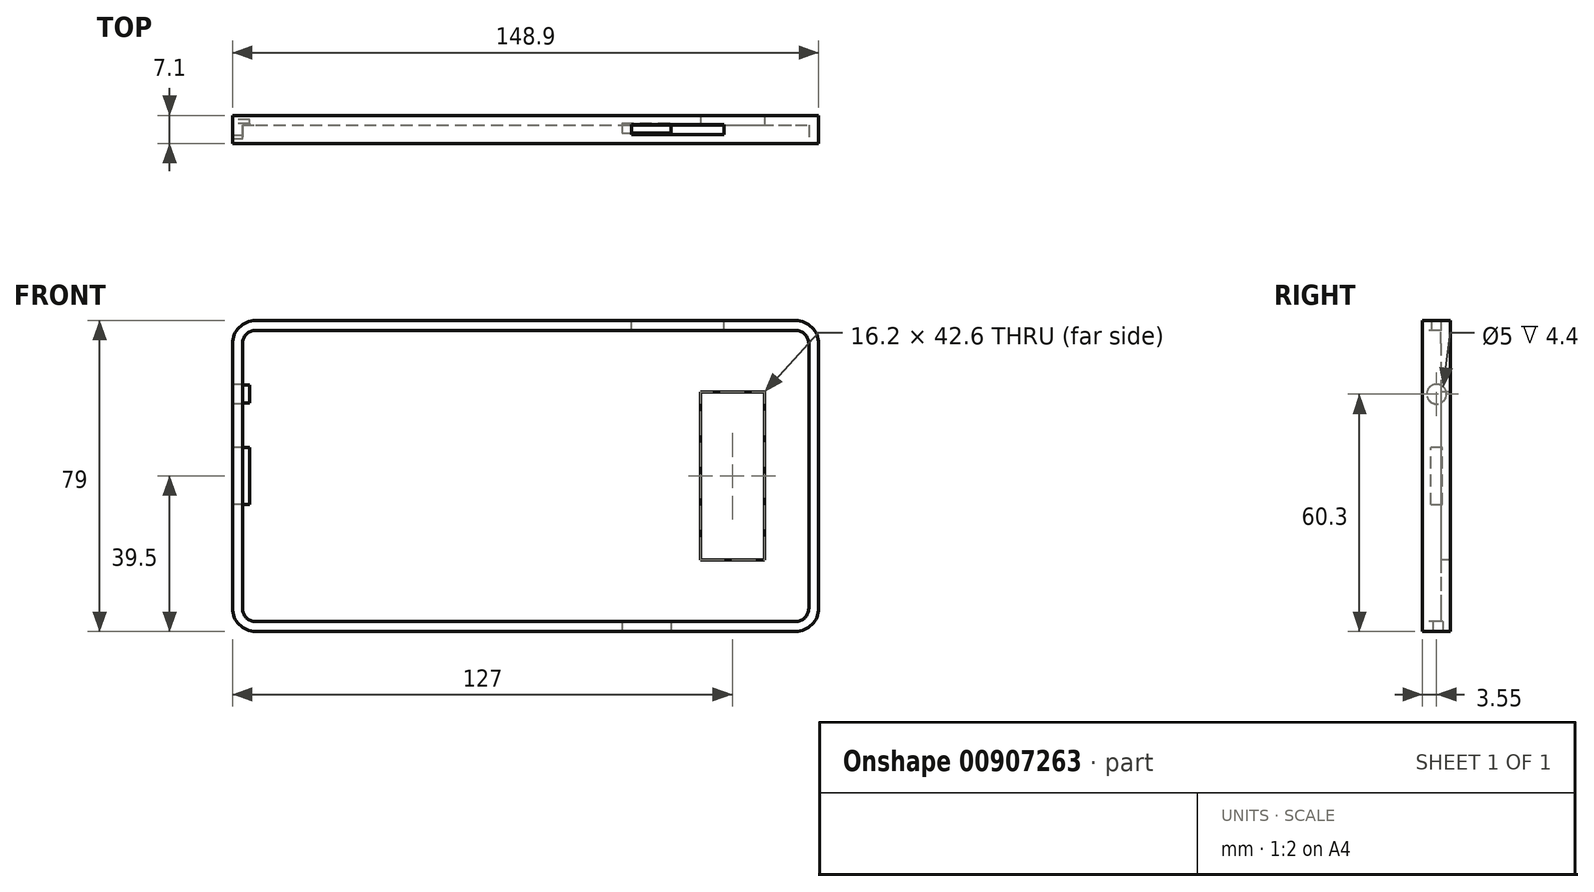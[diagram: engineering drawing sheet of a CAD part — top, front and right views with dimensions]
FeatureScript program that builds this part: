
annotation { "Feature Type Name" : "Feature", "Feature Type Description" : "" }
export const myFeature = defineFeature(function(context is Context, id is Id, definition is map)
    precondition{}
    {
        {
            var Q0;
            Q0=qCreatedBy(makeId("Front.planeOp"),FACE);
            var sketch = newSketch(context, id + "F0", { "sketchPlane" : qUnion([Q0])});
            skLineSegment(sketch, "E0.bottom", {"start": v(-68.55, 39.5) * mm, "end": v(68.55, 39.5) * mm});
            skLineSegment(sketch, "E0.top", {"start": v(-68.55, -39.5) * mm, "end": v(68.55, -39.5) * mm});
            skLineSegment(sketch, "E0.left", {"start": v(-74.45, 33.6) * mm, "end": v(-74.45, -33.6) * mm});
            skLineSegment(sketch, "E0.right", {"start": v(74.45, 33.6) * mm, "end": v(74.45, -33.6) * mm});
            skPoint(sketch, "E0.middle", {"position": v(0, 0) * mm});
            skPoint(sketch, "E1.visualSharp", {"position": v(-74.45, 39.5) * mm});
            skArc(sketch, "E1.filletArc", {"start": v(-68.55, 39.5) * mm, "mid": v(-72.72, 37.77) * mm, "end": v(-74.45, 33.6) * mm});
            skPoint(sketch, "E2.visualSharp", {"position": v(-74.45, -39.5) * mm});
            skArc(sketch, "E2.filletArc", {"start": v(-74.45, -33.6) * mm, "mid": v(-72.72, -37.77) * mm, "end": v(-68.55, -39.5) * mm});
            skPoint(sketch, "E3.visualSharp", {"position": v(74.45, -39.5) * mm});
            skArc(sketch, "E3.filletArc", {"start": v(68.55, -39.5) * mm, "mid": v(72.72, -37.77) * mm, "end": v(74.45, -33.6) * mm});
            skPoint(sketch, "E4.visualSharp", {"position": v(74.45, 39.5) * mm});
            skArc(sketch, "E4.filletArc", {"start": v(74.45, 33.6) * mm, "mid": v(72.72, 37.77) * mm, "end": v(68.55, 39.5) * mm});
            skSolve(sketch);
        }
        {
            var Q0;
            Q0=makeQuery(id+"F0.imprint","IMPRINT",FACE,{"disambiguationData":[TD([[makeQuery(id+"F0.imprint","IMPRINT",EDGE,{"derivedFrom":sQuery(id+"F0.wireOp",EDGE,"E0.bottom")}),-1.0]])]});
            extrude(context, id + "F1", {"entities" : qUnion([Q0]), "oppositeDirection" : true, "depth" : 7.1 * mm, "offsetDistance" : 25 * mm});
        }
        {
            var Q0;
            Q0=makeQuery(id+"F1.opExtrude","CAP_FACE",FACE,{"disambiguationData":[OSD([sQuery(id+"F0.wireOp",EDGE,"E0.bottom"),sQuery(id+"F0.wireOp",EDGE,"E0.top"),sQuery(id+"F0.wireOp",EDGE,"E0.left"),sQuery(id+"F0.wireOp",EDGE,"E0.right"),sQuery(id+"F0.wireOp",EDGE,"E1.filletArc"),sQuery(id+"F0.wireOp",EDGE,"E2.filletArc"),sQuery(id+"F0.wireOp",EDGE,"E3.filletArc"),sQuery(id+"F0.wireOp",EDGE,"E4.filletArc")])],"isStart":true});
            shell(context, id + "F2", {"entities" : qUnion([Q0]), "thickness" : 2.5 * mm});
        }
        {
            var Q0;
            Q0=qCreatedBy(makeId("Front.planeOp"),FACE);
            var sketch = newSketch(context, id + "F3", { "sketchPlane" : qUnion([Q0])});
            skLineSegment(sketch, "E5", {"start": v(44.45, 21.3) * mm, "end": v(44.45, 0) * mm});
            skLineSegment(sketch, "E6", {"start": v(44.45, 21.3) * mm, "end": v(60.65, 21.3) * mm});
            skLineSegment(sketch, "E7", {"start": v(60.65, 21.3) * mm, "end": v(60.65, 0) * mm});
            skLineSegment(sketch, "E8.MirrorCS", {"start": v(44.45, -21.3) * mm, "end": v(44.45, 0) * mm});
            skLineSegment(sketch, "E9.MirrorCS", {"start": v(44.45, -21.3) * mm, "end": v(60.65, -21.3) * mm});
            skLineSegment(sketch, "E10.MirrorCS", {"start": v(60.65, -21.3) * mm, "end": v(60.65, 0) * mm});
            skSolve(sketch);
        }
        {
            var Q0;
            Q0=makeQuery(id+"F3.imprint","IMPRINT",FACE,{"disambiguationData":[TD([[makeQuery(id+"F3.imprint","IMPRINT",EDGE,{"derivedFrom":sQuery(id+"F3.wireOp",EDGE,"E5")}),1.0]])]});
            extrude(context, id + "F4", {"entities" : qUnion([Q0]), "operationType" : NewBodyOperationType.REMOVE, "oppositeDirection" : true, "depth" : 25 * mm, "offsetDistance" : 25 * mm});
        }
        {
            var Q0;
            Q0=makeQuery(id+"F1.opExtrude","SWEPT_FACE",FACE,{"disambiguationData":[OSD([sQuery(id+"F0.wireOp",EDGE,"E0.top")])]});
            var sketch = newSketch(context, id + "F5", { "sketchPlane" : qUnion([Q0])});
            skLineSegment(sketch, "E11", {"start": v(74.45, -3.87) * mm, "end": v(36.95, -3.87) * mm});
            skLineSegment(sketch, "E12", {"start": v(36.95, -3.87) * mm, "end": v(24.45, -3.87) * mm});
            skLineSegment(sketch, "E13", {"start": v(24.45, -3.87) * mm, "end": v(24.45, -2.62) * mm});
            skLineSegment(sketch, "E14", {"start": v(36.95, -3.87) * mm, "end": v(36.95, -5.12) * mm});
            skLineSegment(sketch, "E15.bottom", {"start": v(24.45, -2.62) * mm, "end": v(36.95, -2.62) * mm});
            skLineSegment(sketch, "E15.top", {"start": v(24.45, -5.12) * mm, "end": v(36.95, -5.12) * mm});
            skLineSegment(sketch, "E15.left", {"start": v(24.45, -2.62) * mm, "end": v(24.45, -5.12) * mm});
            skLineSegment(sketch, "E15.right", {"start": v(36.95, -2.62) * mm, "end": v(36.95, -5.12) * mm});
            skSolve(sketch);
        }
        {
            var Q0;
            {var subQ0=sQuery(id+"F5.wireOp",EDGE,"E12");Q0=makeQuery(id+"F5.imprint","IMPRINT",FACE,{"disambiguationData":[TD([[makeQuery(id+"F5.imprint","IMPRINT",EDGE,{"derivedFrom":subQ0}),-1.0]])]});}
            var Q1;
            {var subQ0=sQuery(id+"F5.wireOp",EDGE,"E12");Q1=makeQuery(id+"F5.imprint","IMPRINT",FACE,{"disambiguationData":[TD([[makeQuery(id+"F5.imprint","IMPRINT",EDGE,{"derivedFrom":subQ0}),1.0]])]});}
            extrude(context, id + "F6", {"entities" : qUnion([Q0, Q1]), "operationType" : NewBodyOperationType.REMOVE, "oppositeDirection" : true, "depth" : 2.5 * mm, "offsetDistance" : 25 * mm});
        }
        {
            var Q0;
            Q0=makeQuery(id+"F1.opExtrude","SWEPT_FACE",FACE,{"disambiguationData":[OSD([sQuery(id+"F0.wireOp",EDGE,"E0.bottom")])]});
            var sketch = newSketch(context, id + "F7", { "sketchPlane" : qUnion([Q0])});
            skLineSegment(sketch, "E16", {"start": v(74.45, 3.55) * mm, "end": v(50.45, 3.55) * mm});
            skPoint(sketch, "E16.startSnap0", {"position": v(68.55, 3.55) * mm});
            skLineSegment(sketch, "E17", {"start": v(50.45, 3.55) * mm, "end": v(26.95, 3.55) * mm});
            skLineSegment(sketch, "E18", {"start": v(50.45, 3.55) * mm, "end": v(50.45, 2.3) * mm});
            skLineSegment(sketch, "E19", {"start": v(26.95, 3.55) * mm, "end": v(26.95, 4.8) * mm});
            skLineSegment(sketch, "E20.bottom", {"start": v(50.45, 2.3) * mm, "end": v(26.95, 2.3) * mm});
            skLineSegment(sketch, "E20.top", {"start": v(50.45, 4.8) * mm, "end": v(26.95, 4.8) * mm});
            skLineSegment(sketch, "E20.left", {"start": v(50.45, 2.3) * mm, "end": v(50.45, 4.8) * mm});
            skLineSegment(sketch, "E20.right", {"start": v(26.95, 2.3) * mm, "end": v(26.95, 4.8) * mm});
            skSolve(sketch);
        }
        {
            var Q0;
            {var subQ0=sQuery(id+"F7.wireOp",EDGE,"E17");Q0=makeQuery(id+"F7.imprint","IMPRINT",FACE,{"disambiguationData":[TD([[makeQuery(id+"F7.imprint","IMPRINT",EDGE,{"derivedFrom":subQ0}),1.0]])]});}
            var Q1;
            {var subQ0=sQuery(id+"F7.wireOp",EDGE,"E17");Q1=makeQuery(id+"F7.imprint","IMPRINT",FACE,{"disambiguationData":[TD([[makeQuery(id+"F7.imprint","IMPRINT",EDGE,{"derivedFrom":subQ0}),-1.0]])]});}
            extrude(context, id + "F8", {"entities" : qUnion([Q0, Q1]), "operationType" : NewBodyOperationType.REMOVE, "oppositeDirection" : true, "depth" : 2.5 * mm, "offsetDistance" : 25 * mm});
        }
        {
            var Q0;
            Q0=makeQuery(id+"F1.opExtrude","SWEPT_FACE",FACE,{"disambiguationData":[OSD([sQuery(id+"F0.wireOp",EDGE,"E0.left")])]});
            var sketch = newSketch(context, id + "F9", { "sketchPlane" : qUnion([Q0])});
            skLineSegment(sketch, "E21", {"start": v(0, 0) * mm, "end": v(-7.1, 0) * mm});
            skLineSegment(sketch, "E22", {"start": v(-3.55, 0) * mm, "end": v(-3.55, -7.25) * mm});
            skLineSegment(sketch, "E23", {"start": v(-3.55, -7.25) * mm, "end": v(-5.05, -7.25) * mm});
            skLineSegment(sketch, "E24", {"start": v(-3.55, -7.25) * mm, "end": v(-2.05, -7.25) * mm});
            skLineSegment(sketch, "E25", {"start": v(-5.05, -7.25) * mm, "end": v(-5.05, 0) * mm});
            skLineSegment(sketch, "E26", {"start": v(-2.05, -7.25) * mm, "end": v(-2.05, 0) * mm});
            skLineSegment(sketch, "E27.MirrorCS", {"start": v(-2.05, 7.25) * mm, "end": v(-2.05, 0) * mm});
            skLineSegment(sketch, "E28.MirrorCS", {"start": v(-5.05, 7.25) * mm, "end": v(-5.05, 0) * mm});
            skLineSegment(sketch, "E29.MirrorCS", {"start": v(-3.55, 7.25) * mm, "end": v(-5.05, 7.25) * mm});
            skLineSegment(sketch, "E30.MirrorCS", {"start": v(-3.55, 7.25) * mm, "end": v(-2.05, 7.25) * mm});
            skPoint(sketch, "E31.startSnap0", {"position": v(-3.55, 33.6) * mm});
            skCircle(sketch, "E32", {"center": v(-3.55, 20.8) * mm, "radius": 2.5 * mm});
            skSolve(sketch);
        }
        {
            var Q0;
            {var subQ0=sQuery(id+"F9.wireOp",EDGE,"E22");Q0=makeQuery(id+"F9.imprint","IMPRINT",FACE,{"disambiguationData":[TD([[makeQuery(id+"F9.imprint","IMPRINT",EDGE,{"derivedFrom":subQ0}),-1.0]])]});}
            var Q1;
            {var subQ0=sQuery(id+"F9.wireOp",EDGE,"E22");Q1=makeQuery(id+"F9.imprint","IMPRINT",FACE,{"disambiguationData":[TD([[makeQuery(id+"F9.imprint","IMPRINT",EDGE,{"derivedFrom":subQ0}),1.0]])]});}
            var Q2;
            {var subQ1=sQuery(id+"F9.wireOp",EDGE,"E27.MirrorCS");Q2=makeQuery(id+"F9.imprint","IMPRINT",FACE,{"disambiguationData":[TD([[makeQuery(id+"F9.imprint","IMPRINT",EDGE,{"derivedFrom":subQ1}),-1.0]])]});}
            var Q3;
            Q3=makeQuery(id+"F9.imprint","IMPRINT",FACE,{"disambiguationData":[TD([[makeQuery(id+"F9.imprint","IMPRINT",EDGE,{"derivedFrom":sQuery(id+"F9.wireOp",EDGE,"E32")}),1.0]])]});
            extrude(context, id + "F10", {"entities" : qUnion([Q0, Q1, Q2, Q3]), "operationType" : NewBodyOperationType.REMOVE, "oppositeDirection" : true, "depth" : 4.4 * mm, "offsetDistance" : 25 * mm});
        }
    });
